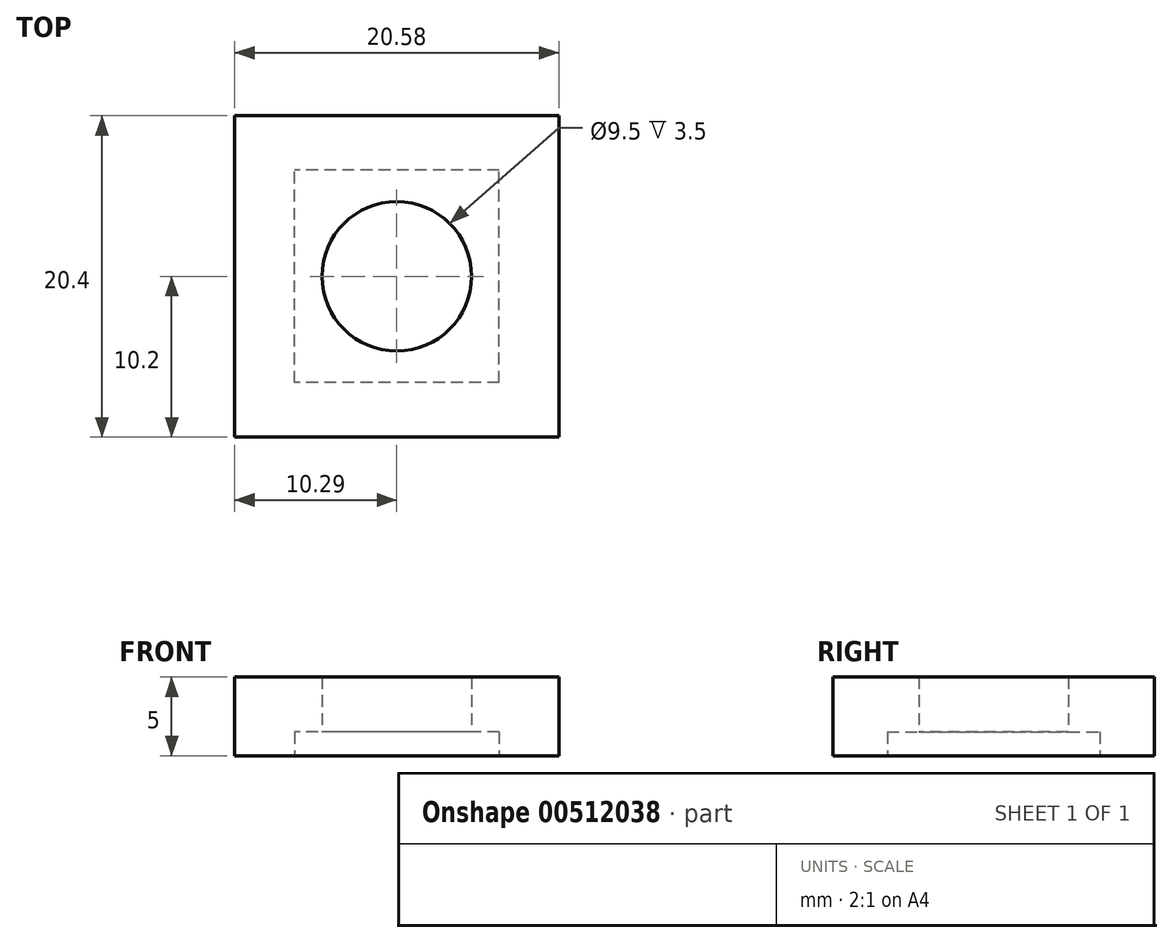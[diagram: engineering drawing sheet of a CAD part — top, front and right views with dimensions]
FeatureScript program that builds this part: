
annotation { "Feature Type Name" : "Feature", "Feature Type Description" : "" }
export const myFeature = defineFeature(function(context is Context, id is Id, definition is map)
    precondition{}
    {
        {
            var Q0;
            Q0=qCreatedBy(makeId("Top.planeOp"),FACE);
            var sketch = newSketch(context, id + "F0", { "sketchPlane" : qUnion([Q0])});
            skCircle(sketch, "E0", {"center": v(0, 0) * mm, "radius": 4.75 * mm});
            skLineSegment(sketch, "E1.bottom", {"start": v(-10.29, 10.2) * mm, "end": v(10.29, 10.2) * mm});
            skLineSegment(sketch, "E1.top", {"start": v(-10.29, -10.2) * mm, "end": v(10.29, -10.2) * mm});
            skLineSegment(sketch, "E1.left", {"start": v(-10.29, 10.2) * mm, "end": v(-10.29, -10.2) * mm});
            skLineSegment(sketch, "E1.right", {"start": v(10.29, 10.2) * mm, "end": v(10.29, -10.2) * mm});
            skLineSegment(sketch, "E2.bottom", {"start": v(6.5, -6.75) * mm, "end": v(-6.5, -6.75) * mm});
            skLineSegment(sketch, "E2.top", {"start": v(6.5, 6.75) * mm, "end": v(-6.5, 6.75) * mm});
            skLineSegment(sketch, "E2.left", {"start": v(6.5, -6.75) * mm, "end": v(6.5, 6.75) * mm});
            skLineSegment(sketch, "E2.right", {"start": v(-6.5, -6.75) * mm, "end": v(-6.5, 6.75) * mm});
            skSolve(sketch);
        }
        {
            var Q0;
            Q0=makeQuery(id+"F0.imprint","IMPRINT",FACE,{"disambiguationData":[TD([[makeQuery(id+"F0.imprint","IMPRINT",EDGE,{"derivedFrom":sQuery(id+"F0.wireOp",EDGE,"E0")}),-1.0]])]});
            var Q1;
            Q1=makeQuery(id+"F0.imprint","IMPRINT",FACE,{"disambiguationData":[TD([[makeQuery(id+"F0.imprint","IMPRINT",EDGE,{"derivedFrom":sQuery(id+"F0.wireOp",EDGE,"E1.bottom")}),-1.0]])]});
            extrude(context, id + "F1", {"entities" : qUnion([Q0, Q1]), "depth" : 5 * mm, "offsetDistance" : 25 * mm});
        }
        {
            var Q0;
            Q0=makeQuery(id+"F0.imprint","IMPRINT",FACE,{"disambiguationData":[TD([[makeQuery(id+"F0.imprint","IMPRINT",EDGE,{"derivedFrom":sQuery(id+"F0.wireOp",EDGE,"E0")}),-1.0]])]});
            extrude(context, id + "F2", {"entities" : qUnion([Q0]), "operationType" : NewBodyOperationType.REMOVE, "depth" : 1.5 * mm, "offsetDistance" : 25 * mm});
        }
    });
